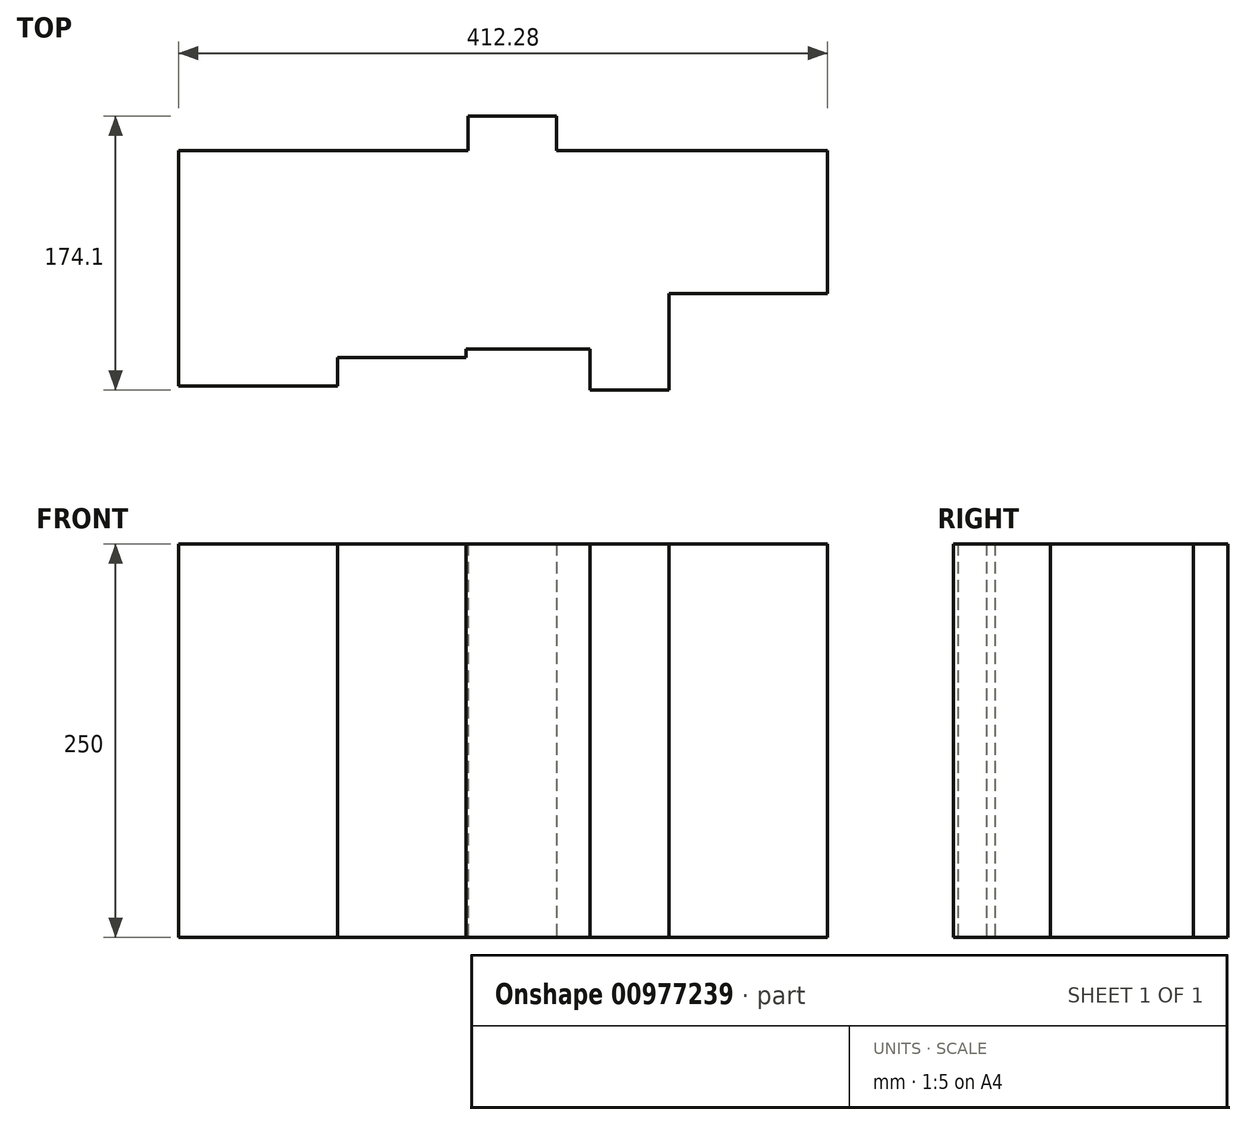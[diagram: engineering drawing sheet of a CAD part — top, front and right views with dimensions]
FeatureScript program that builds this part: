
annotation { "Feature Type Name" : "Feature", "Feature Type Description" : "" }
export const myFeature = defineFeature(function(context is Context, id is Id, definition is map)
    precondition{}
    {
        {
            var Q0;
            Q0=qCreatedBy(makeId("Top.planeOp"),FACE);
            var sketch = newSketch(context, id + "F0", { "sketchPlane" : qUnion([Q0])});
            skLineSegment(sketch, "E0", {"start": v(0, 0) * mm, "end": v(101.09, 0) * mm});
            skLineSegment(sketch, "E1", {"start": v(101.09, 0) * mm, "end": v(101.09, 17.96) * mm});
            skLineSegment(sketch, "E2", {"start": v(101.09, 17.96) * mm, "end": v(182.6, 17.96) * mm});
            skLineSegment(sketch, "E3", {"start": v(182.6, 17.96) * mm, "end": v(182.6, 23.4) * mm});
            skLineSegment(sketch, "E4", {"start": v(182.6, 23.4) * mm, "end": v(261.41, 23.4) * mm});
            skLineSegment(sketch, "E5", {"start": v(261.41, 23.4) * mm, "end": v(261.41, -2.77) * mm});
            skLineSegment(sketch, "E6", {"start": v(261.41, -2.77) * mm, "end": v(311.44, -2.77) * mm});
            skLineSegment(sketch, "E7", {"start": v(311.44, -2.77) * mm, "end": v(311.44, 58.66) * mm});
            skLineSegment(sketch, "E8", {"start": v(311.44, 58.66) * mm, "end": v(412.28, 58.66) * mm});
            skLineSegment(sketch, "E9", {"start": v(412.28, 58.66) * mm, "end": v(412.28, 149.44) * mm});
            skLineSegment(sketch, "E10", {"start": v(412.28, 149.44) * mm, "end": v(240.17, 149.44) * mm});
            skLineSegment(sketch, "E11", {"start": v(240.17, 149.44) * mm, "end": v(240.17, 171.33) * mm});
            skLineSegment(sketch, "E12", {"start": v(240.17, 171.33) * mm, "end": v(183.76, 171.33) * mm});
            skLineSegment(sketch, "E13", {"start": v(183.76, 171.33) * mm, "end": v(183.76, 149.44) * mm});
            skLineSegment(sketch, "E14", {"start": v(183.76, 149.44) * mm, "end": v(0, 149.44) * mm});
            skLineSegment(sketch, "E15", {"start": v(0, 149.44) * mm, "end": v(0, 0) * mm});
            skSolve(sketch);
        }
        {
            var Q0;
            Q0 = qSketchRegion(id + "F0", true);
            extrude(context, id + "F1", {"entities" : qUnion([Q0]), "depth" : 250 * mm, "offsetDistance" : 25 * mm});
        }
    });
